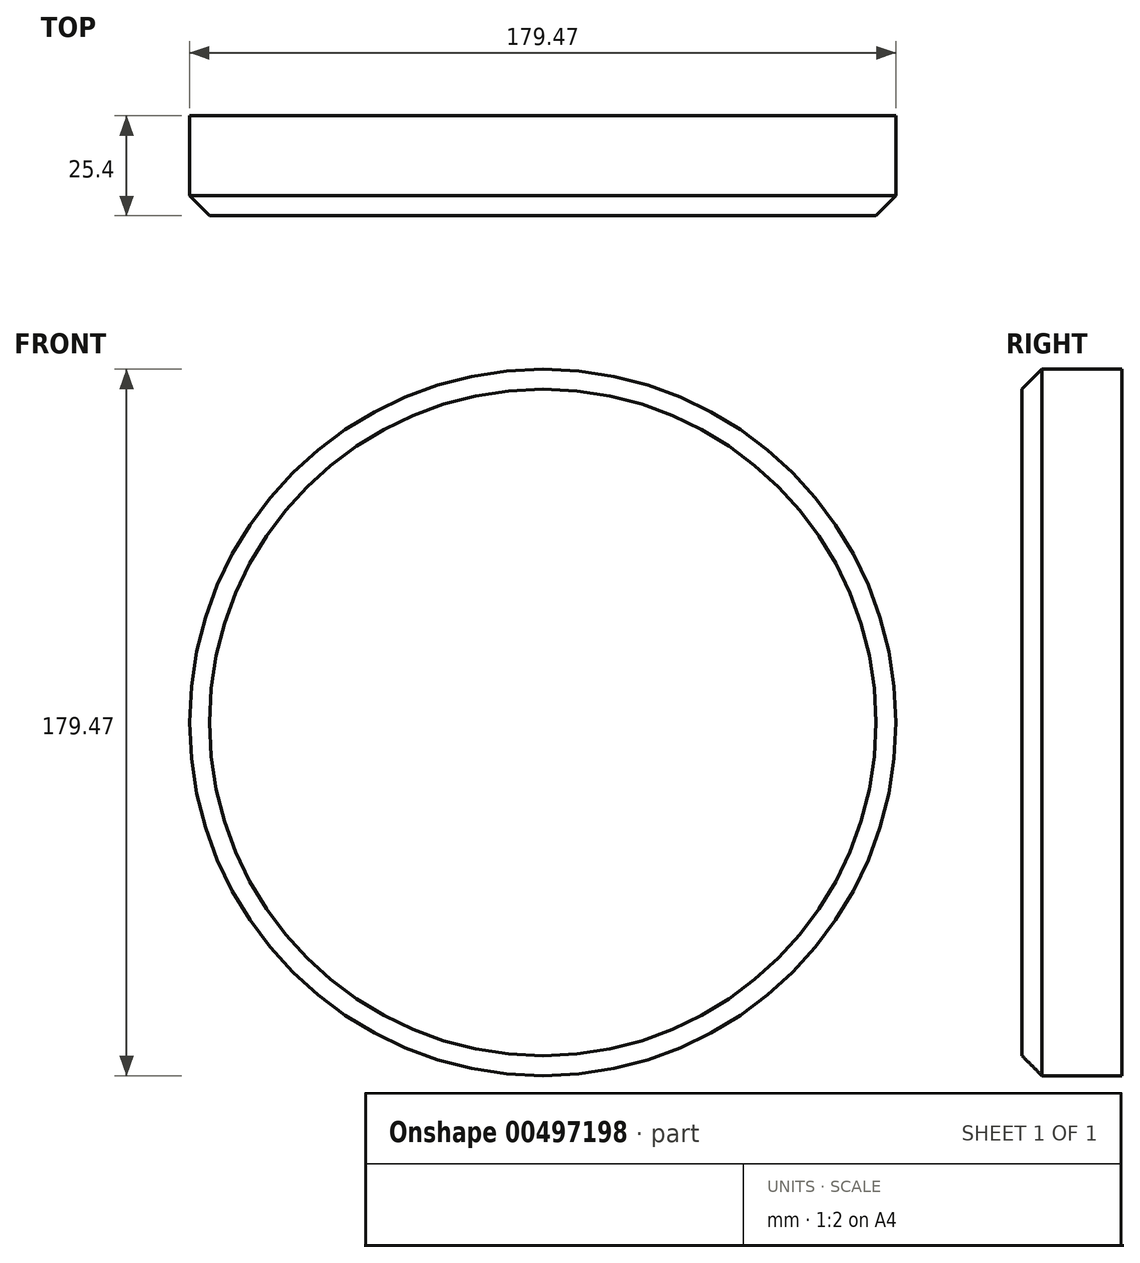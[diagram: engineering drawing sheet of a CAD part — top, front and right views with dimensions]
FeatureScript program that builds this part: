
annotation { "Feature Type Name" : "Feature", "Feature Type Description" : "" }
export const myFeature = defineFeature(function(context is Context, id is Id, definition is map)
    precondition{}
    {
        {
            var Q0;
            Q0=qCreatedBy(makeId("Front.planeOp"),FACE);
            var sketch = newSketch(context, id + "F0", { "sketchPlane" : qUnion([Q0])});
            skCircle(sketch, "E0", {"center": v(-57.85, 68.9) * mm, "radius": 89.74 * mm});
            skSolve(sketch);
        }
        {
            var Q0;
            Q0 = qSketchRegion(id + "F0", true);
            extrude(context, id + "F1", {"entities" : qUnion([Q0]), "endBound" : BoundingType.SYMMETRIC, "depth" : 25.4 * mm});
        }
        {
            var Q0;
            Q0=makeQuery(id+"F1.opExtrude","CAP_EDGE",EDGE,{"disambiguationData":[OSD([sQuery(id+"F0.wireOp",EDGE,"E0")])],"isStart":false});
            chamfer(context, id + "F2", {"entities" : qUnion([Q0]), "width" : 5.08 * mm, "tangentPropagation" : true});
        }
    });
